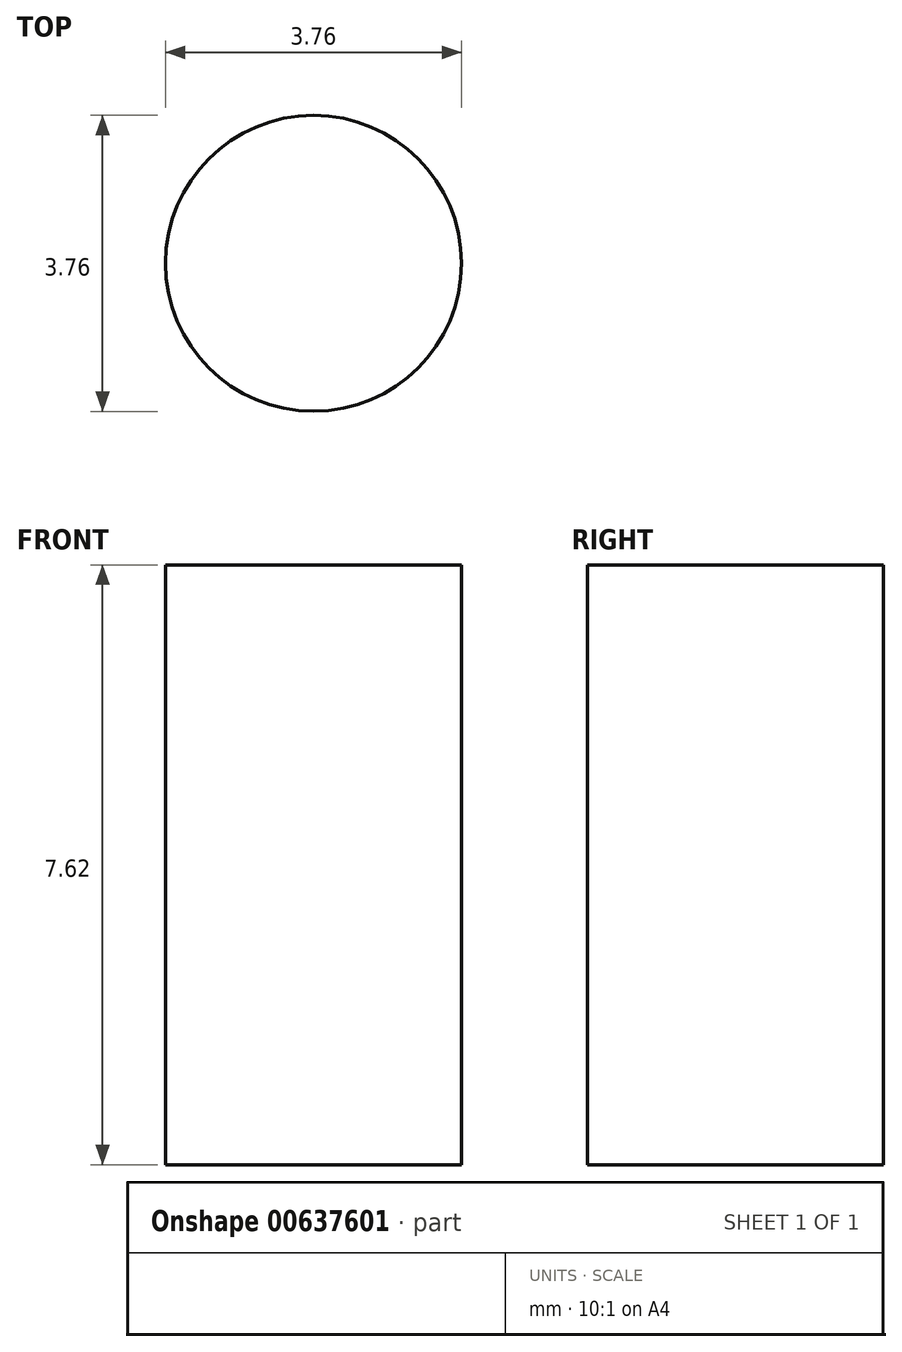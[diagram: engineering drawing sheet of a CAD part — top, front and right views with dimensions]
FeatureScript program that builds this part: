
annotation { "Feature Type Name" : "Feature", "Feature Type Description" : "" }
export const myFeature = defineFeature(function(context is Context, id is Id, definition is map)
    precondition{}
    {
        {
            var Q0;
            Q0=qCreatedBy(makeId("Top.planeOp"),FACE);
            var sketch = newSketch(context, id + "F0", { "sketchPlane" : qUnion([Q0])});
            skCircle(sketch, "E0", {"center": v(0, 0) * mm, "radius": 1.88 * mm});
            skSolve(sketch);
        }
        {
            var Q0;
            Q0 = qSketchRegion(id + "F0", true);
            extrude(context, id + "F1", {"entities" : qUnion([Q0]), "depth" : 7.62 * mm, "offsetDistance" : 25.4 * mm});
        }
    });
